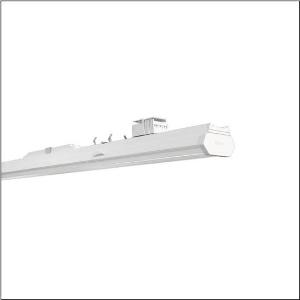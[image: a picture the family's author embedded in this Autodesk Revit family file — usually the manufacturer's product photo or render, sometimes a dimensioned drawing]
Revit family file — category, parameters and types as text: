
# Revit family: licross_11_protected_mo_51td1bcn485g
name_source: partatom
category: Lighting Fixtures
units: mm (PartAtom-declared; Revit-internal decimal feet)

## family parameters
Cut with Voids When Loaded = No
Host = Face
Light Source = No
Part Type = Normal
Room Calculation Point = No
Round Connector Dimension = Use Diameter
Shared = No

## types (1)
- --- (1 x LED, 8520 lm, 49.4 W, 4000K)
    Apparent Load = 49 VA
    CIE Flux Codes = 54 82 95 97 100
    Color Rendering = 80
    Color Temperature = 4000K
    Default Elevation = 1800 mm
    Description = Licross 11 Protected MO, luminaire insert, of sheet steel, galvanised, coil coated, white, length: 1.500mm, width: 90mm, height: 101mm, LED rated luminous flux: 8.520lm, light colour: 840, SDCM (Standard Deviation of Colour Matching)MacAdam ≤ 2 SDCM (initial), control gear: ON/OFF Multilumen, CLOi, with plug, 3-pole, with phase selection, mains connection: 220..240V, AC, 50/60Hz, start of lifetime: 49W, end of service life: 55W, internal wiring halogen-free, primary optical cover: cover, of PMMA, light emission: direct distribution, primary light characteristic: symmetric, protection rating (complete): IP54, insulation class (complete): insulation class I (protective earthing), certification: CE, ENEC, VDE, UKCA, protection symbol: D if used in an environment with non-conductive dust loads with corresponding accessories, impact resistance: IK06, permissible ambient temperature for indoor applications: -35..+40°C, corresponds to IFS (International Featured Standards) requirements for safety and quality in the food industry, reducing of maximum allowable ambient temperature of 5°C with ceiling mounting, LABS conformity tested according to VDMA 24364:2018-05, The light source and the operating device comply with the requirements of the Ecodesign Regulation (EU) 2019/2020 and are replaceable in accordance with this regulation, packaging unit: 1 piece
    Height = 92 mm
    Lamp = 1 x LED
    Lamp Light Flux = 8520 lm
    Lamp Power = 49.4 W
    Lamp count = 1
    Length = 1500 mm
    Luminous efficacy = 172 lm/W
    Manufacturer = Siteco
    ModVariant = No
    Model = 51TD1BCN485G
    Mounting Place = Ceiling
    Mounting Type = Pendant
    Number of Poles = 1
    OnlyDefault = Yes
    Power Factor = 1
    Product Name = Licross 11 Protected MO
    Product group = luminaire insert | ceiling pendant
    ProductGroupID = 901
    Protection Class = Protection class I
    Protection Degree = IP 54
    RLX_Detail_Level = 1
    RLX_Emergency_Light_Flux = 0 lm
    RLX_Emergency_Type = 0
    RLX_Emergency_Type_DB = No
    RlxData = <blob elided: 22409 chars, md5=da22f1a5>
    Socket = socket
    Standby Power = 0 W
    System Light Flux = 8520 lm
    System Power = 49 W
    Type Comments = factory setting: luminous flux: 100 % | (A | C | E) | 113 mA
    Type Image = l_1256145.jpg
    URL = http://relux.com
    VarID = @adj_000967
    Voltage = 0 V
    Weight = 0.00 kg
    Width = 88 mm

## geometry (parser evidence)
native form markers: Blend x4, Sweep x12
no freeform markers — native parametric forms only
